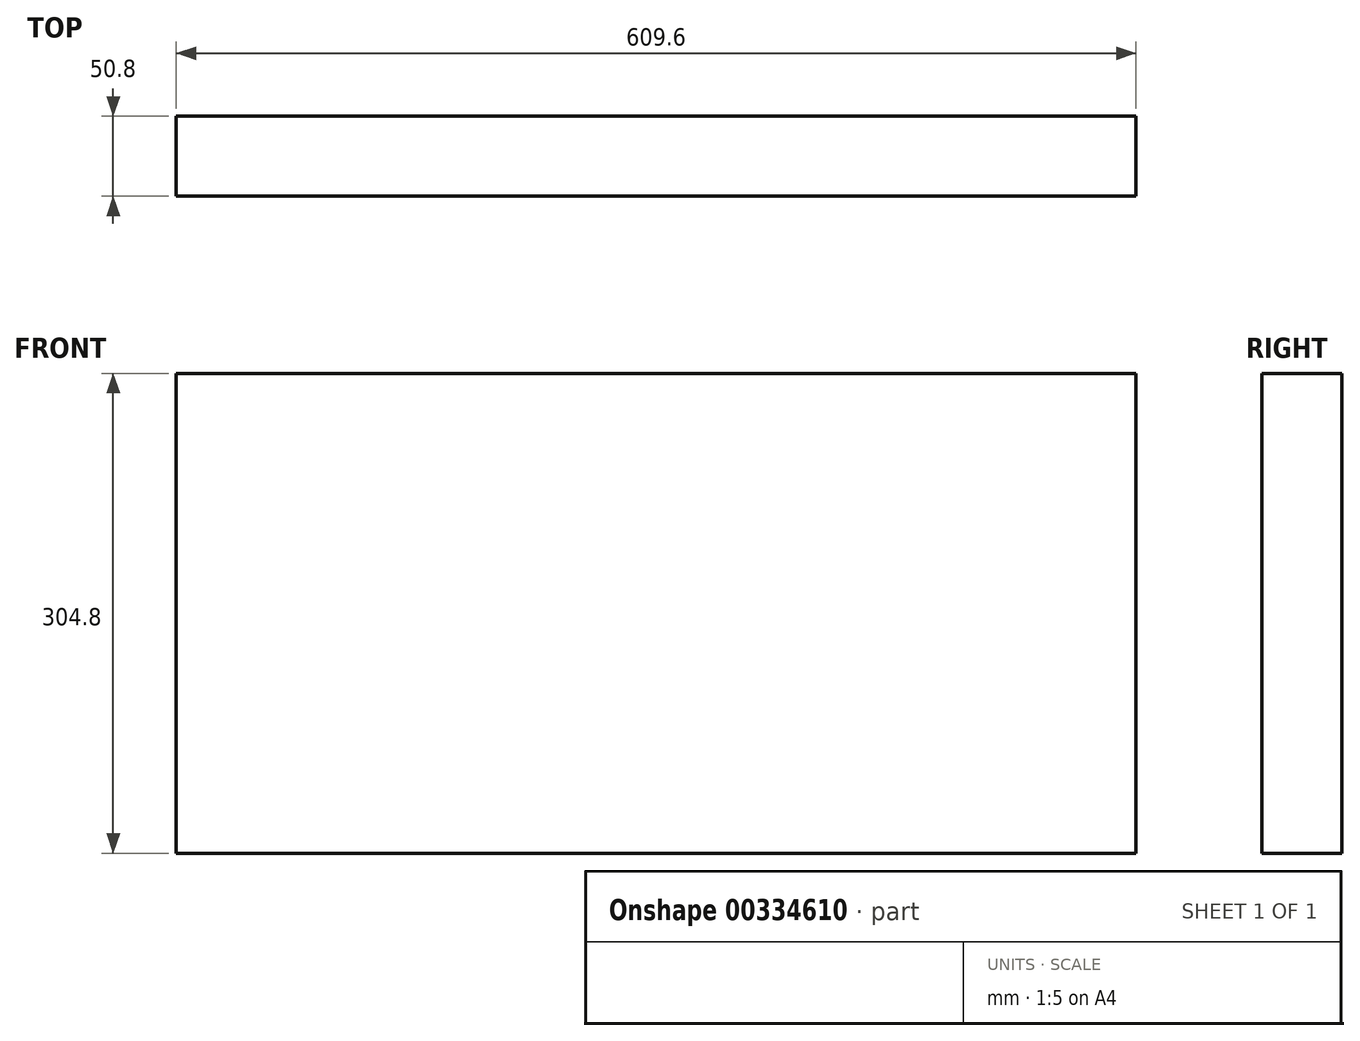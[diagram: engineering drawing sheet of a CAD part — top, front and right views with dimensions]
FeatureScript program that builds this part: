
annotation { "Feature Type Name" : "Feature", "Feature Type Description" : "" }
export const myFeature = defineFeature(function(context is Context, id is Id, definition is map)
    precondition{}
    {
        {
            var Q0;
            Q0=qCreatedBy(makeId("Front.planeOp"),FACE);
            var sketch = newSketch(context, id + "F0", { "sketchPlane" : qUnion([Q0])});
            skLineSegment(sketch, "E0.bottom", {"start": v(-236.64, 137.51) * mm, "end": v(372.96, 137.51) * mm});
            skLineSegment(sketch, "E0.top", {"start": v(-236.64, -167.29) * mm, "end": v(372.96, -167.29) * mm});
            skLineSegment(sketch, "E0.left", {"start": v(-236.64, 137.51) * mm, "end": v(-236.64, -167.29) * mm});
            skLineSegment(sketch, "E0.right", {"start": v(372.96, 137.51) * mm, "end": v(372.96, -167.29) * mm});
            skSolve(sketch);
        }
        {
            var Q0;
            Q0=makeQuery(id+"F0.imprint","IMPRINT",FACE,{"disambiguationData":[TD([[makeQuery(id+"F0.imprint","IMPRINT",EDGE,{"derivedFrom":sQuery(id+"F0.wireOp",EDGE,"E0.bottom")}),-1.0]])]});
            extrude(context, id + "F1", {"entities" : qUnion([Q0]), "endBound" : BoundingType.SYMMETRIC, "depth" : 50.8 * mm});
        }
    });
